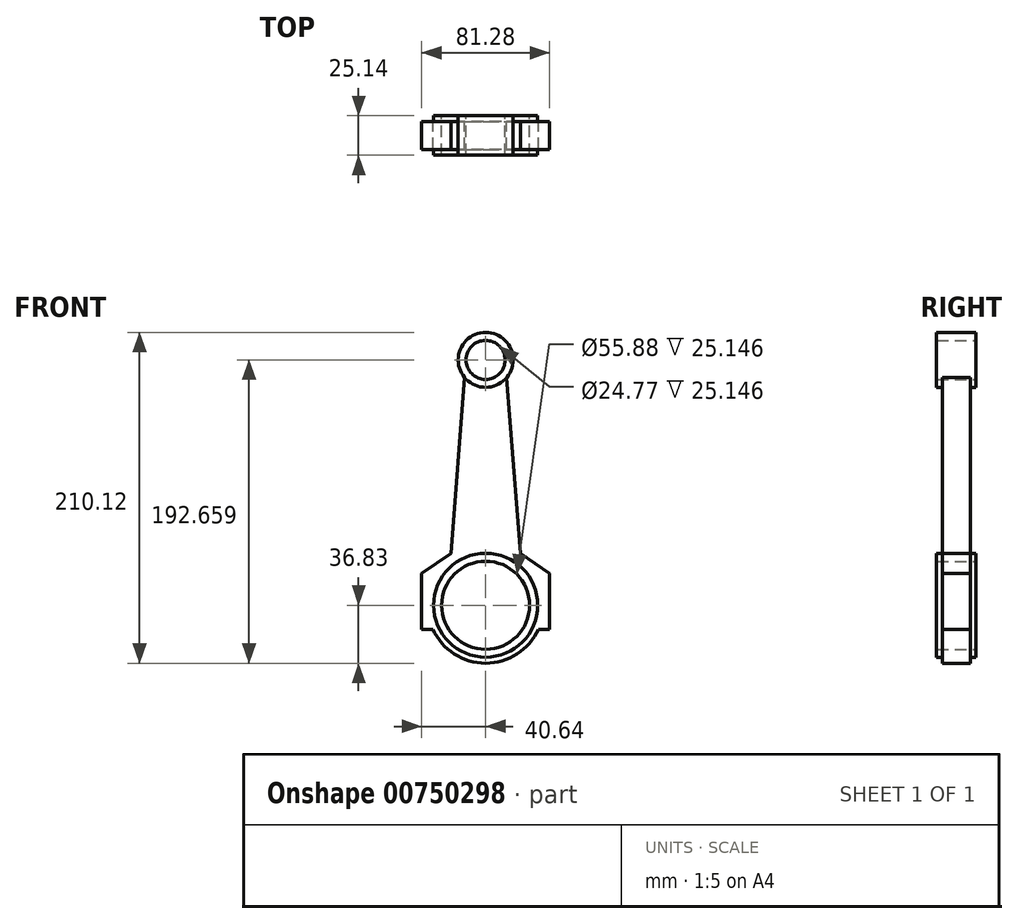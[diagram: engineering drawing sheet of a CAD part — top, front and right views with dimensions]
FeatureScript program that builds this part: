
annotation { "Feature Type Name" : "Feature", "Feature Type Description" : "" }
export const myFeature = defineFeature(function(context is Context, id is Id, definition is map)
    precondition{}
    {
        {
            var Q0;
            Q0=qCreatedBy(makeId("Front.planeOp"),FACE);
            var sketch = newSketch(context, id + "F0", { "sketchPlane" : qUnion([Q0])});
            skCircle(sketch, "E0", {"center": v(0, 0) * mm, "radius": 27.94 * mm});
            skCircle(sketch, "E1", {"center": v(0, 155.83) * mm, "radius": 12.38 * mm});
            skCircle(sketch, "E2.0", {"center": v(0, 0) * mm, "radius": 33.02 * mm});
            skCircle(sketch, "E3.0", {"center": v(0, 155.83) * mm, "radius": 17.46 * mm});
            skArc(sketch, "E4.0", {"start": v(-33.53, -15.24) * mm, "mid": v(0, -36.83) * mm, "end": v(33.53, -15.24) * mm});
            skLineSegment(sketch, "E5", {"start": v(0, 0) * mm, "end": v(-40.64, 0) * mm});
            skLineSegment(sketch, "E6.MirrorCS", {"start": v(0, 0) * mm, "end": v(40.64, 0) * mm});
            skLineSegment(sketch, "E7", {"start": v(-40.64, 0) * mm, "end": v(-40.64, 20.32) * mm});
            skLineSegment(sketch, "E8", {"start": v(-40.64, 20.32) * mm, "end": v(-22.1, 33.02) * mm});
            skLineSegment(sketch, "E9", {"start": v(-22.1, 33.02) * mm, "end": v(-12.42, 155.83) * mm});
            skLineSegment(sketch, "E10.MirrorCS", {"start": v(22.1, 33.02) * mm, "end": v(12.42, 155.83) * mm});
            skLineSegment(sketch, "E11.MirrorCS", {"start": v(40.64, 20.32) * mm, "end": v(22.1, 33.02) * mm});
            skLineSegment(sketch, "E12.MirrorCS", {"start": v(40.64, 0) * mm, "end": v(40.64, 20.32) * mm});
            skLineSegment(sketch, "E13", {"start": v(-40.64, 0) * mm, "end": v(-40.64, -15.24) * mm});
            skLineSegment(sketch, "E14", {"start": v(-40.64, -15.24) * mm, "end": v(-33.53, -15.24) * mm});
            skLineSegment(sketch, "E15.MirrorCS", {"start": v(40.64, 0) * mm, "end": v(40.64, -15.24) * mm});
            skLineSegment(sketch, "E16.MirrorCS", {"start": v(40.64, -15.24) * mm, "end": v(33.53, -15.24) * mm});
            skSolve(sketch);
        }
        {
            var Q0;
            {var subQ0=sQuery(id+"F0.wireOp",EDGE,"E5");var subQ1=sQuery(id+"F0.wireOp",EDGE,"E0");var subQ2=makeQuery(id+"F0.imprint","INTERSECT",VERTEX,{"derivedFrom":[subQ1,subQ0]});Q0=makeQuery(id+"F0.imprint","IMPRINT",FACE,{"disambiguationData":[TD([[makeQuery(id+"F0.imprint","IMPRINT",EDGE,{"disambiguationData":[TD([[subQ2,1.0]])],"derivedFrom":subQ1}),-1.0]])]});}
            extrude(context, id + "F1", {"entities" : qUnion([Q0]), "endBound" : BoundingType.SYMMETRIC, "depth" : 25.15 * mm, "offsetDistance" : 25.4 * mm});
        }
        {
            var Q0;
            {var subQ0=sQuery(id+"F0.wireOp",EDGE,"E7");Q0=makeQuery(id+"F0.imprint","IMPRINT",FACE,{"disambiguationData":[TD([[makeQuery(id+"F0.imprint","IMPRINT",EDGE,{"derivedFrom":subQ0}),-1.0]])]});}
            extrude(context, id + "F2", {"entities" : qUnion([Q0]), "operationType" : NewBodyOperationType.ADD, "endBound" : BoundingType.SYMMETRIC, "depth" : 17.78 * mm, "offsetDistance" : 25.4 * mm});
        }
        {
            var Q0;
            Q0=makeQuery(id+"F0.imprint","IMPRINT",FACE,{"disambiguationData":[TD([[makeQuery(id+"F0.imprint","IMPRINT",EDGE,{"derivedFrom":sQuery(id+"F0.wireOp",EDGE,"E1")}),-1.0]])]});
            extrude(context, id + "F3", {"entities" : qUnion([Q0]), "operationType" : NewBodyOperationType.ADD, "endBound" : BoundingType.SYMMETRIC, "depth" : 25.15 * mm, "offsetDistance" : 25.4 * mm});
        }
        {
            var Q0;
            {var subQ0=sQuery(id+"F0.wireOp",EDGE,"E5");var subQ1=sQuery(id+"F0.wireOp",EDGE,"E0");var subQ2=makeQuery(id+"F0.imprint","INTERSECT",VERTEX,{"derivedFrom":[subQ1,subQ0]});Q0=makeQuery(id+"F0.imprint","IMPRINT",FACE,{"disambiguationData":[TD([[makeQuery(id+"F0.imprint","IMPRINT",EDGE,{"disambiguationData":[TD([[subQ2,-1.0]])],"derivedFrom":subQ1}),-1.0]])]});}
            extrude(context, id + "F4", {"entities" : qUnion([Q0]), "endBound" : BoundingType.SYMMETRIC, "depth" : 25.15 * mm, "offsetDistance" : 25.4 * mm});
        }
        {
            var Q0;
            Q0=makeQuery(id+"F0.imprint","IMPRINT",FACE,{"disambiguationData":[TD([[makeQuery(id+"F0.imprint","IMPRINT",EDGE,{"derivedFrom":sQuery(id+"F0.wireOp",EDGE,"E4.0")}),1.0]])]});
            extrude(context, id + "F5", {"entities" : qUnion([Q0]), "operationType" : NewBodyOperationType.ADD, "endBound" : BoundingType.SYMMETRIC, "depth" : 17.78 * mm, "offsetDistance" : 25.4 * mm});
        }
    });
